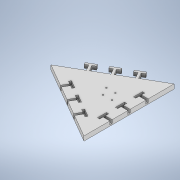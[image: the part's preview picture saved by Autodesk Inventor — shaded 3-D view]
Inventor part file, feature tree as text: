
AUTODESK INVENTOR PART (.ipt)
format: ipt  version: 2022.3 (Build 263350000, 350)  size: 350,208 bytes
history: native  units: mm
features: extrude x6, sketch x4, hole x1, projected_geometry x1
ambient origin geometry x8: Origin, YZ Plane, XZ Plane, XY Plane, X Axis, Y Axis, Z Axis, Center Point
bodies: Solid1 (feature_tree)
feature tree (12):
  sketch  "Sketch1"  dims[d1=200.0mm d2=35.0mm]
  extrude  "Extrusion1"  Depth=35.0mm
  extrude  "Extrusion2"  Depth=5.0mm
  extrude  "Extrusion3"  Depth=40.0mm
  extrude  "Extrusion4"  Depth=10.0mm TaperAngle=0.0deg
  sketch  "Sketch3"  dims[d5=20.0mm d6=30.0mm d8=40.0mm d9=30.0mm d11=40.0mm]
  extrude  "Extrusion6"  Depth=2.5mm TaperAngle=0.0deg
  extrude  "Extrusion7"  Depth=22.0mm
  hole  "Hole1"  [1 undecoded]
  sketch  "Sketch2"  dims[d3=5.0mm d4=5.0mm]
  projected_geometry  "Projected Loop1"
  sketch  "Sketch4"  dims[d14=10.0mm d15=0.0mm d16=10.0mm d17=0.0mm d18=2.5mm d19=0.0mm d20=22.0mm d21=3.0mm d22=1.5mm d23=0.0mm d24=15.0mm d25=120.0deg d26=10.0mm d27=5.0mm d28=20.0mm d29=90.0deg d30=5.0mm d31=2.5mm d32=5.0mm d33=20.0mm d35=120.0deg d37=30.0mm d39=40.0mm d40=30.0mm d42=40.0mm d45=30.0mm d47=40.0mm d48=30.0mm d50=40.0mm d55=10.0mm d56=0.0mm d57=10.0mm d58=0.0mm d59=40.0mm d60=2.2mm d61=6.0mm d62=3.1mm d63=4.1mm d64=90.0deg d65=2.2mm d66=0.0mm d67=1.0mm d68=1.0mm d69=1.0mm d70=0.15mm d71=2.2mm d72=0.375mm d73=14.3117mm d74=0.75mm d75=20.594885mm d76=0.0625mm d77=0.75mm d78=0.375mm]
note: 1 required parameter value undecoded (feature->parameter linkage not recoverable at this tier; creation-order binding heuristic only, values carry confidence <= 0.55)
